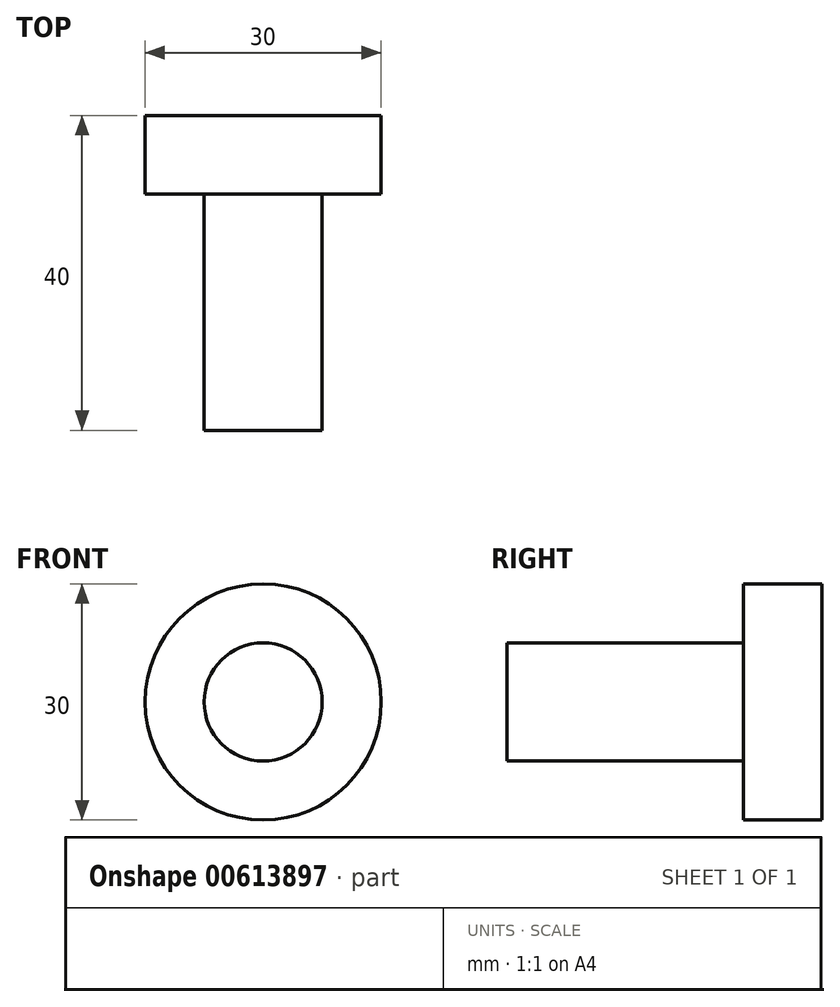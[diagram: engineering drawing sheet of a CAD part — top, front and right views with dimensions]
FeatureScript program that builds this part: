
annotation { "Feature Type Name" : "Feature", "Feature Type Description" : "" }
export const myFeature = defineFeature(function(context is Context, id is Id, definition is map)
    precondition{}
    {
        {
            var Q0;
            Q0=qCreatedBy(makeId("Front.planeOp"),FACE);
            var sketch = newSketch(context, id + "F0", { "sketchPlane" : qUnion([Q0])});
            skCircle(sketch, "E0", {"center": v(0, 0) * mm, "radius": 15 * mm});
            skCircle(sketch, "E1", {"center": v(0, 0) * mm, "radius": 7.5 * mm});
            skSolve(sketch);
        }
        {
            var Q0;
            Q0=qCreatedBy(makeId("Front.planeOp"),FACE);
            var sketch = newSketch(context, id + "F1", { "sketchPlane" : qUnion([Q0])});
            skCircle(sketch, "E2", {"center": v(0, 0) * mm, "radius": 7.5 * mm});
            skSolve(sketch);
        }
        {
            var Q0;
            Q0=makeQuery(id+"F0.imprint","IMPRINT",FACE,{"disambiguationData":[TD([[makeQuery(id+"F0.imprint","IMPRINT",EDGE,{"derivedFrom":sQuery(id+"F0.wireOp",EDGE,"E0")}),1.0]])]});
            extrude(context, id + "F2", {"entities" : qUnion([Q0]), "depth" : 10 * mm, "offsetDistance" : 25 * mm});
        }
        {
            var Q0;
            Q0=makeQuery(id+"F1.imprint","IMPRINT",FACE,{"disambiguationData":[TD([[makeQuery(id+"F1.imprint","IMPRINT",EDGE,{"derivedFrom":sQuery(id+"F1.wireOp",EDGE,"E2")}),1.0]])]});
            extrude(context, id + "F3", {"entities" : qUnion([Q0]), "operationType" : NewBodyOperationType.ADD, "depth" : 40 * mm, "offsetDistance" : 25 * mm});
        }
    });
